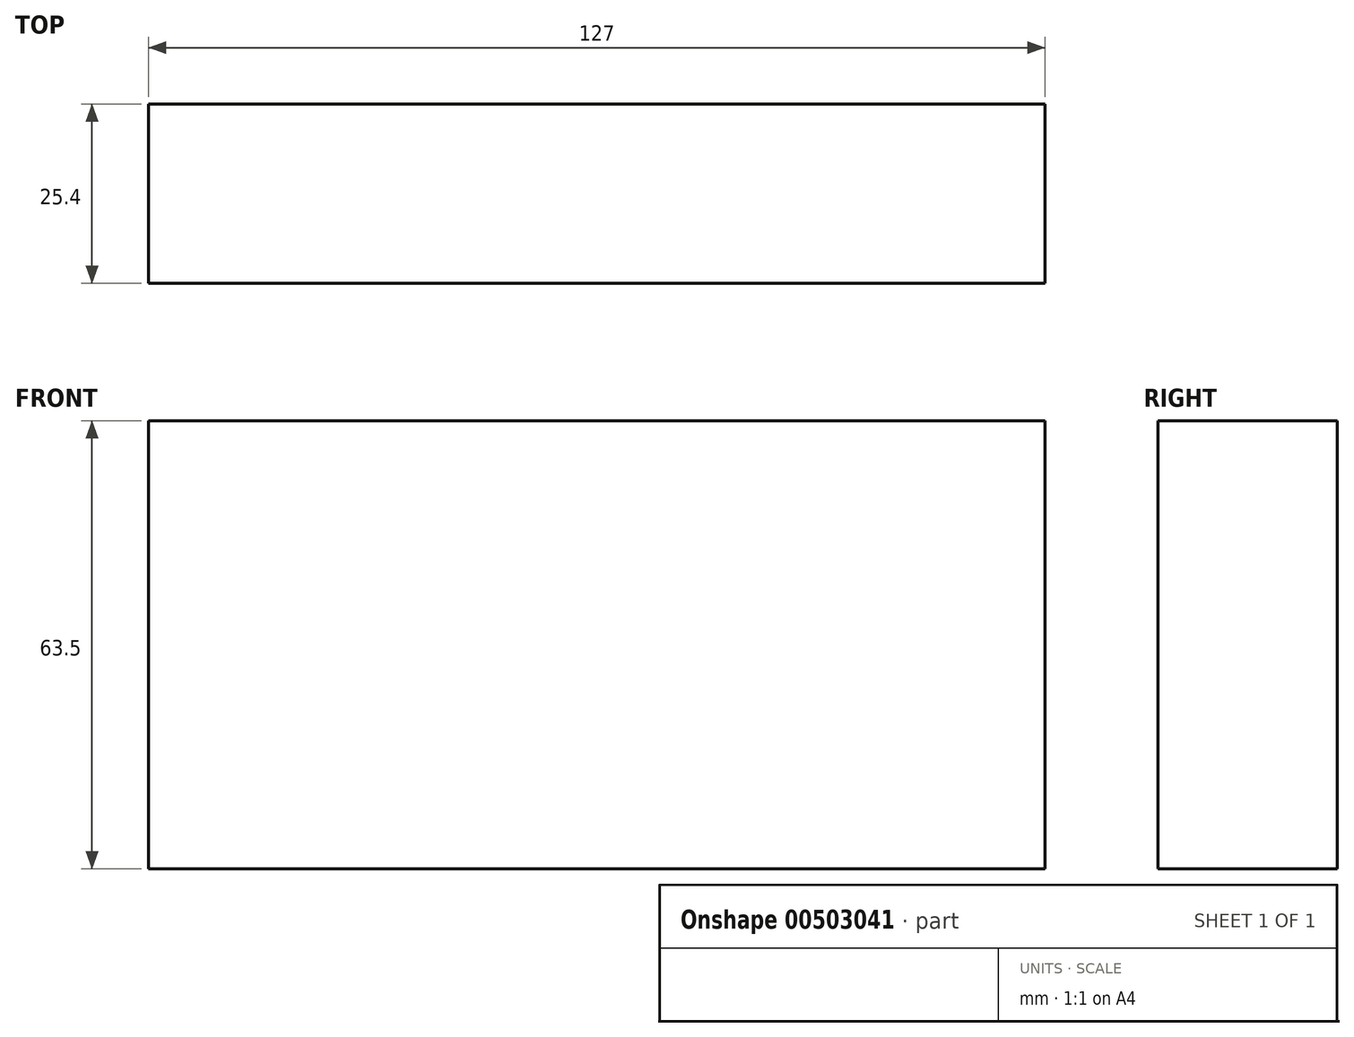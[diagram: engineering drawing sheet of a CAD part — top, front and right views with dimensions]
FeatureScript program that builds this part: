
annotation { "Feature Type Name" : "Feature", "Feature Type Description" : "" }
export const myFeature = defineFeature(function(context is Context, id is Id, definition is map)
    precondition{}
    {
        {
            var Q0;
            Q0=qCreatedBy(makeId("Front.planeOp"),FACE);
            var sketch = newSketch(context, id + "F0", { "sketchPlane" : qUnion([Q0])});
            skLineSegment(sketch, "E0", {"start": v(-63.27, 19.89) * mm, "end": v(63.73, 19.89) * mm});
            skLineSegment(sketch, "E1", {"start": v(63.73, 19.89) * mm, "end": v(63.73, -43.61) * mm});
            skLineSegment(sketch, "E2", {"start": v(63.73, -43.61) * mm, "end": v(-63.27, -43.61) * mm});
            skLineSegment(sketch, "E3", {"start": v(-63.27, -43.61) * mm, "end": v(-63.27, 19.89) * mm});
            skSolve(sketch);
        }
        {
            var Q0;
            Q0=makeQuery(id+"F0.imprint","IMPRINT",FACE,{"disambiguationData":[TD([[makeQuery(id+"F0.imprint","IMPRINT",EDGE,{"derivedFrom":sQuery(id+"F0.wireOp",EDGE,"E0")}),-1.0]])]});
            extrude(context, id + "F1", {"entities" : qUnion([Q0]), "depth" : 25.4 * mm});
        }
    });
